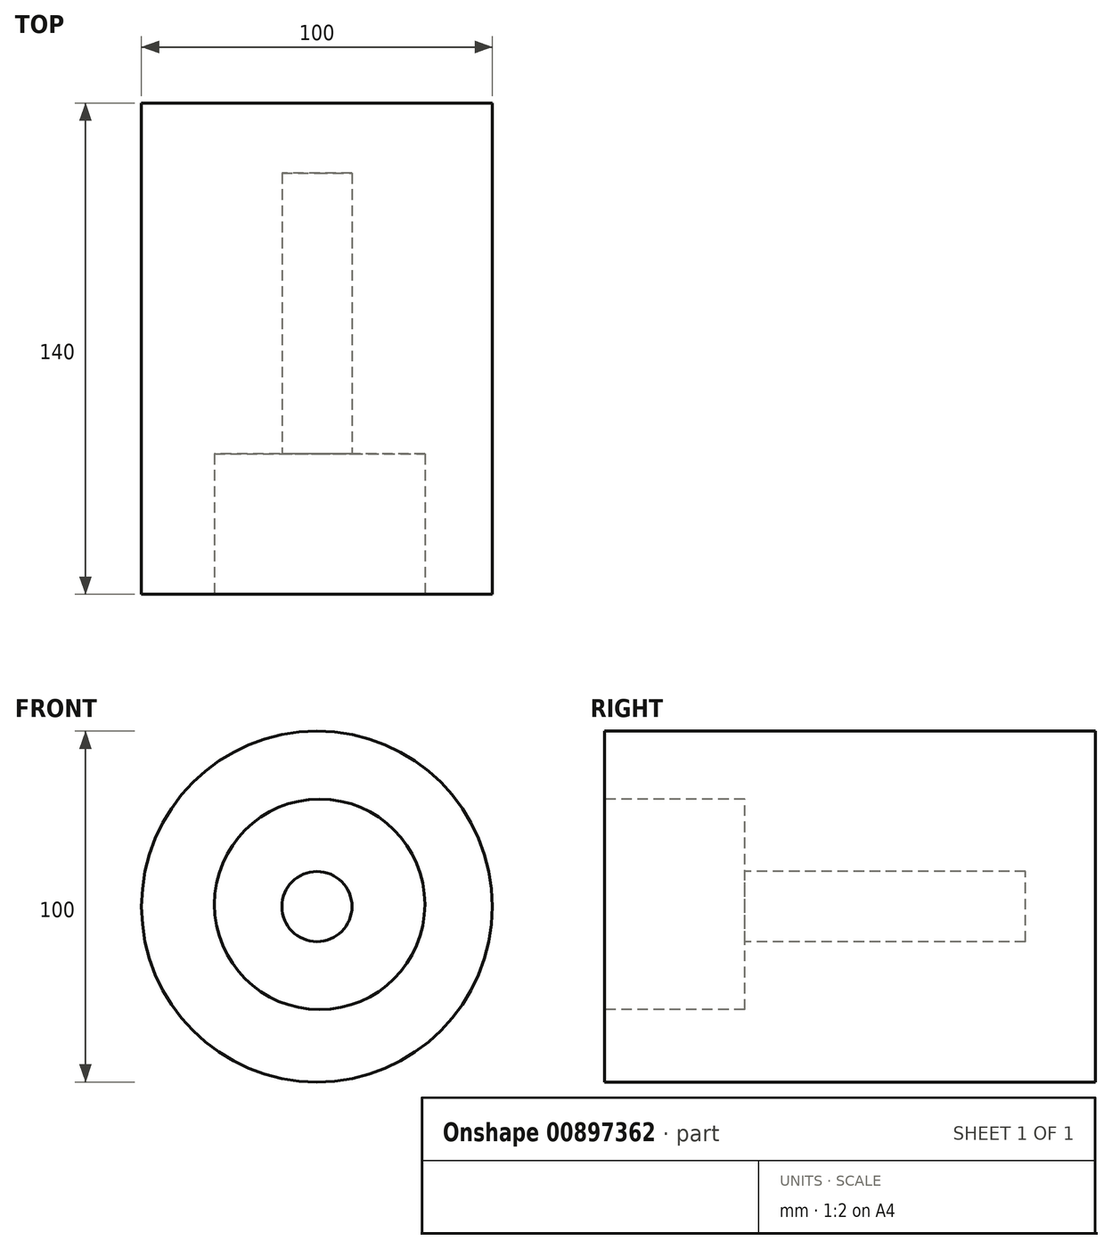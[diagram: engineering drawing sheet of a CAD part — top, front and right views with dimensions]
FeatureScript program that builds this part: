
annotation { "Feature Type Name" : "Feature", "Feature Type Description" : "" }
export const myFeature = defineFeature(function(context is Context, id is Id, definition is map)
    precondition{}
    {
        {
            var Q0;
            Q0=qCreatedBy(makeId("Front.planeOp"),FACE);
            var sketch = newSketch(context, id + "F0", { "sketchPlane" : qUnion([Q0])});
            skCircle(sketch, "E0", {"center": v(0, 0) * mm, "radius": 50 * mm});
            skSolve(sketch);
        }
        {
            var Q0;
            Q0=makeQuery(id+"F0.imprint","IMPRINT",FACE,{"disambiguationData":[TD([[makeQuery(id+"F0.imprint","IMPRINT",EDGE,{"derivedFrom":sQuery(id+"F0.wireOp",EDGE,"E0")}),1.0]])]});
            extrude(context, id + "F1", {"entities" : qUnion([Q0]), "depth" : 140 * mm, "offsetDistance" : 25.4 * mm});
        }
        {
            var Q0;
            Q0=makeQuery(id+"F1.opExtrude","CAP_FACE",FACE,{"disambiguationData":[OSD([sQuery(id+"F0.wireOp",EDGE,"E0")])],"isStart":false});
            var sketch = newSketch(context, id + "F2", { "sketchPlane" : qUnion([Q0])});
            skCircle(sketch, "E1", {"center": v(0.79, 0.63) * mm, "radius": 30 * mm});
            skSolve(sketch);
        }
        {
            var Q0;
            Q0=makeQuery(id+"F2.imprint","IMPRINT",FACE,{"disambiguationData":[TD([[makeQuery(id+"F2.imprint","IMPRINT",EDGE,{"derivedFrom":sQuery(id+"F2.wireOp",EDGE,"E1")}),1.0]])]});
            extrude(context, id + "F3", {"entities" : qUnion([Q0]), "operationType" : NewBodyOperationType.REMOVE, "oppositeDirection" : true, "depth" : 40 * mm, "offsetDistance" : 25.4 * mm});
        }
        {
            var Q0;
            Q0=makeQuery(id+"F3.boolean.opBoolean","COPY",FACE,{"derivedFrom":makeQuery(id+"F3.opExtrude","CAP_FACE",FACE,{"disambiguationData":[OSD([sQuery(id+"F2.wireOp",EDGE,"E1")])],"isStart":false})});
            var sketch = newSketch(context, id + "F4", { "sketchPlane" : qUnion([Q0])});
            skCircle(sketch, "E2", {"center": v(0, 0) * mm, "radius": 10 * mm});
            skSolve(sketch);
        }
        {
            var Q0;
            Q0 = qSketchRegion(id + "F4", true);
            extrude(context, id + "F5", {"entities" : qUnion([Q0]), "operationType" : NewBodyOperationType.REMOVE, "oppositeDirection" : true, "depth" : 80 * mm, "offsetDistance" : 25.4 * mm});
        }
    });
